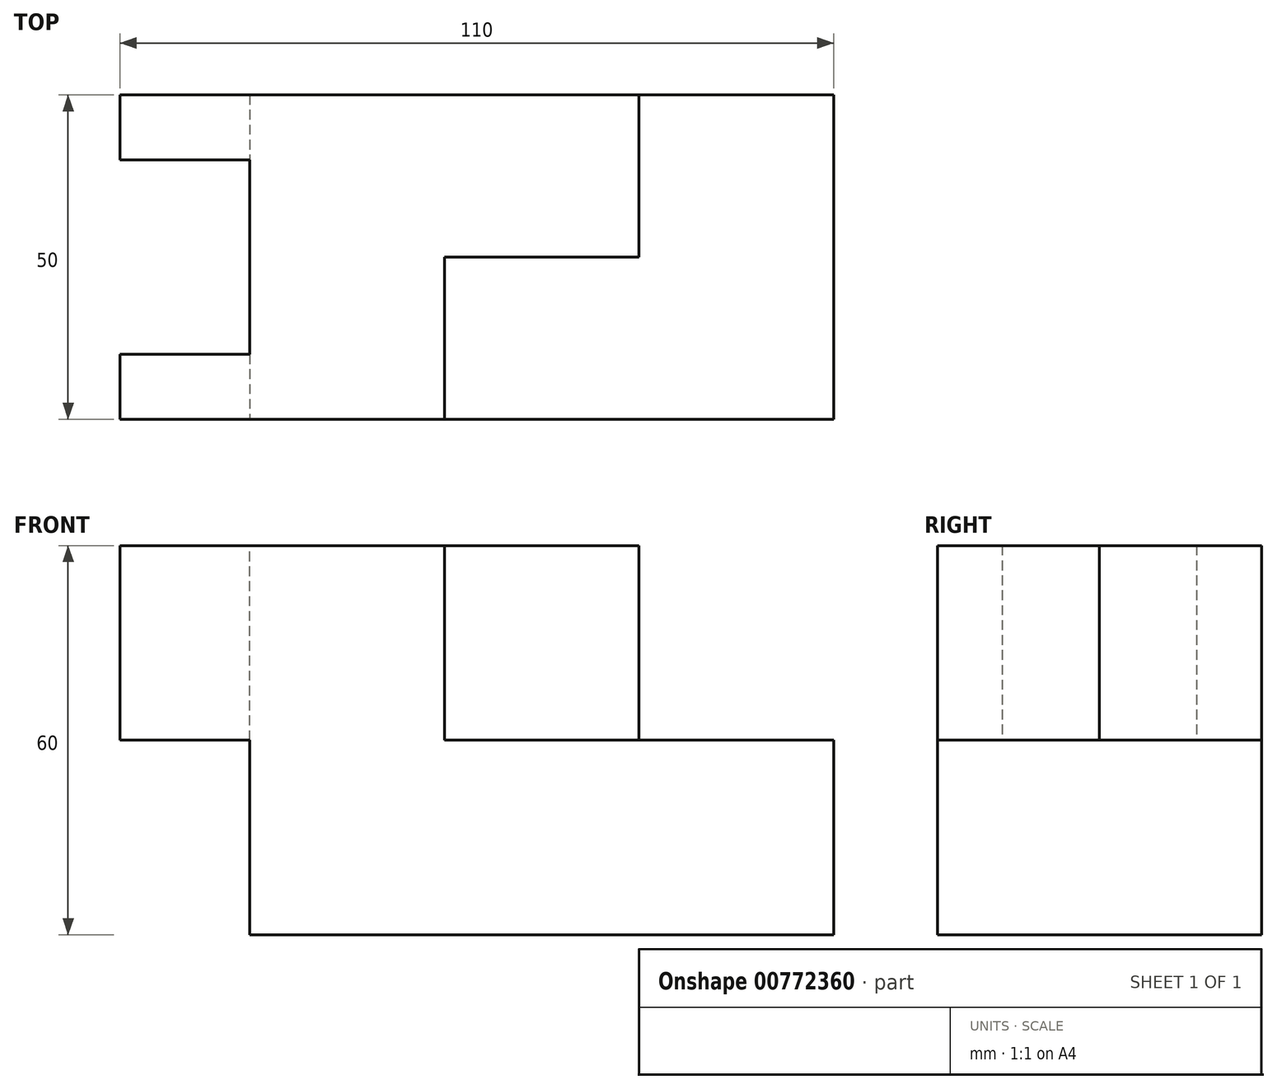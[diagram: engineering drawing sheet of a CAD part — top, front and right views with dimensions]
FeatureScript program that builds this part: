
annotation { "Feature Type Name" : "Feature", "Feature Type Description" : "" }
export const myFeature = defineFeature(function(context is Context, id is Id, definition is map)
    precondition{}
    {
        {
            var Q0;
            Q0=qCreatedBy(makeId("Front.planeOp"),FACE);
            var sketch = newSketch(context, id + "F0", { "sketchPlane" : qUnion([Q0])});
            skLineSegment(sketch, "E0", {"start": v(0, 0) * mm, "end": v(90, 0) * mm});
            skLineSegment(sketch, "E1", {"start": v(90, 0) * mm, "end": v(90, 30) * mm});
            skLineSegment(sketch, "E2", {"start": v(90, 30) * mm, "end": v(60, 30) * mm});
            skLineSegment(sketch, "E3", {"start": v(60, 30) * mm, "end": v(60, 60) * mm});
            skLineSegment(sketch, "E4", {"start": v(60, 60) * mm, "end": v(-20, 60) * mm});
            skLineSegment(sketch, "E5", {"start": v(-20, 60) * mm, "end": v(-20, 30) * mm});
            skLineSegment(sketch, "E6", {"start": v(-20, 30) * mm, "end": v(0, 30) * mm});
            skLineSegment(sketch, "E7", {"start": v(0, 30) * mm, "end": v(0, 0) * mm});
            skLineSegment(sketch, "E8", {"start": v(60, 30) * mm, "end": v(30, 30) * mm});
            skLineSegment(sketch, "E9", {"start": v(30, 30) * mm, "end": v(30, 60) * mm});
            skLineSegment(sketch, "E10", {"start": v(0, 30) * mm, "end": v(0, 60) * mm});
            skSolve(sketch);
        }
        {
            var Q0;
            Q0 = qSketchRegion(id + "F0", true);
            extrude(context, id + "F1", {"entities" : qUnion([Q0]), "endBound" : BoundingType.SYMMETRIC, "oppositeDirection" : true, "depth" : 50 * mm, "offsetDistance" : 25 * mm});
        }
        {
            var Q0;
            {var subQ0=sQuery(id+"F0.wireOp",EDGE,"E3");Q0=makeQuery(id+"F0.imprint","IMPRINT",FACE,{"disambiguationData":[TD([[makeQuery(id+"F0.imprint","IMPRINT",EDGE,{"derivedFrom":subQ0}),1.0]])]});}
            extrude(context, id + "F2", {"entities" : qUnion([Q0]), "operationType" : NewBodyOperationType.REMOVE, "depth" : 25 * mm, "offsetDistance" : 25 * mm});
        }
        {
            var Q0;
            {var subQ0=sQuery(id+"F0.wireOp",EDGE,"E5");Q0=makeQuery(id+"F0.imprint","IMPRINT",FACE,{"disambiguationData":[TD([[makeQuery(id+"F0.imprint","IMPRINT",EDGE,{"derivedFrom":subQ0}),1.0]])]});}
            extrude(context, id + "F3", {"entities" : qUnion([Q0]), "operationType" : NewBodyOperationType.REMOVE, "endBound" : BoundingType.SYMMETRIC, "oppositeDirection" : true, "depth" : 30 * mm, "offsetDistance" : 25 * mm});
        }
    });
